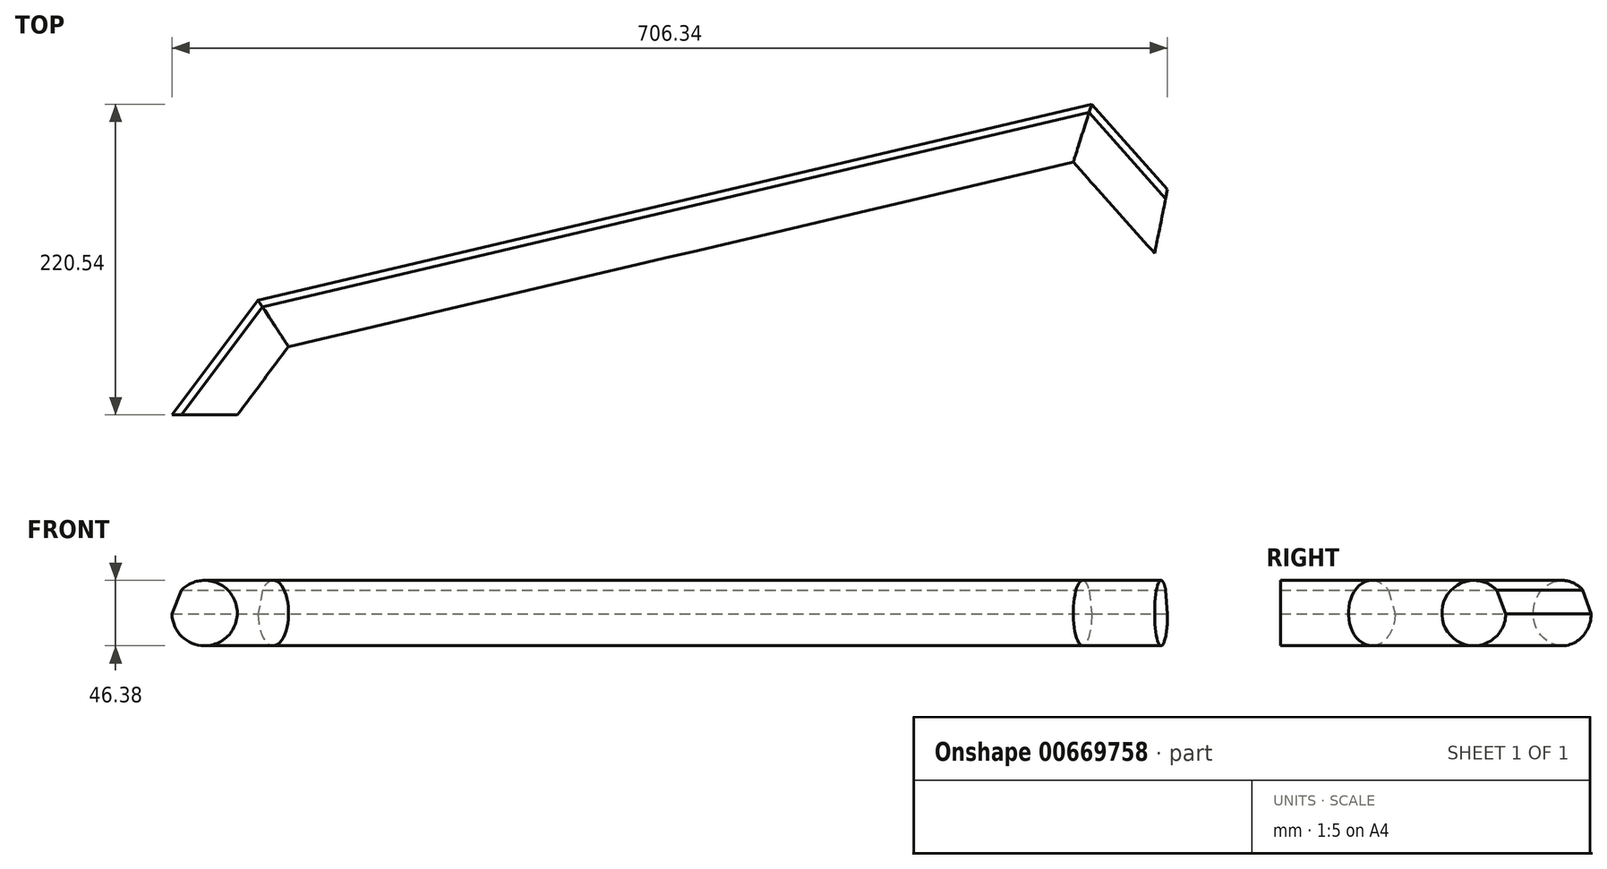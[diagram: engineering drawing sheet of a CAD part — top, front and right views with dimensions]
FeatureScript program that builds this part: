
annotation { "Feature Type Name" : "Feature", "Feature Type Description" : "" }
export const myFeature = defineFeature(function(context is Context, id is Id, definition is map)
    precondition{}
    {
        {
            var Q0;
            Q0=qCreatedBy(makeId("Front.planeOp"),FACE);
            var sketch = newSketch(context, id + "F0", { "sketchPlane" : qUnion([Q0])});
            skArc(sketch, "E0", {"start": v(-23.33, 0) * mm, "mid": v(21.4, -7.92) * mm, "end": v(-16.57, 17.02) * mm});
            skLineSegment(sketch, "E1", {"start": v(-23.33, 0) * mm, "end": v(-16.57, 17.02) * mm});
            skLineSegment(sketch, "E2", {"start": v(-32.34, -40.68) * mm, "end": v(44.52, -40.68) * mm});
            skSolve(sketch);
        }
        {
            var Q0;
            Q0=qCreatedBy(makeId("Top.planeOp"),FACE);
            var sketch = newSketch(context, id + "F1", { "sketchPlane" : qUnion([Q0])});
            skLineSegment(sketch, "E3", {"start": v(0, 0) * mm, "end": v(48.61, 64.78) * mm});
            skLineSegment(sketch, "E4", {"start": v(48.61, 64.78) * mm, "end": v(622.63, 199.84) * mm});
            skLineSegment(sketch, "E5", {"start": v(622.63, 199.84) * mm, "end": v(678.37, 137.14) * mm});
            skSolve(sketch);
        }
        {
            var Q0;
            Q0=makeQuery(id+"F0.imprint","IMPRINT",FACE,{"disambiguationData":[TD([[makeQuery(id+"F0.imprint","IMPRINT",EDGE,{"derivedFrom":sQuery(id+"F0.wireOp",EDGE,"E0")}),1.0]])]});
            var Q1;
            Q1=sQuery(id+"F1.wireOp",EDGE,"E3");
            var Q2;
            Q2=sQuery(id+"F1.wireOp",EDGE,"E4");
            var Q3;
            Q3=sQuery(id+"F1.wireOp",EDGE,"E5");
            sweep(context, id + "F2", {"profiles" : qUnion([Q0]), "path" : qUnion([Q1, Q2, Q3])});
        }
    });
